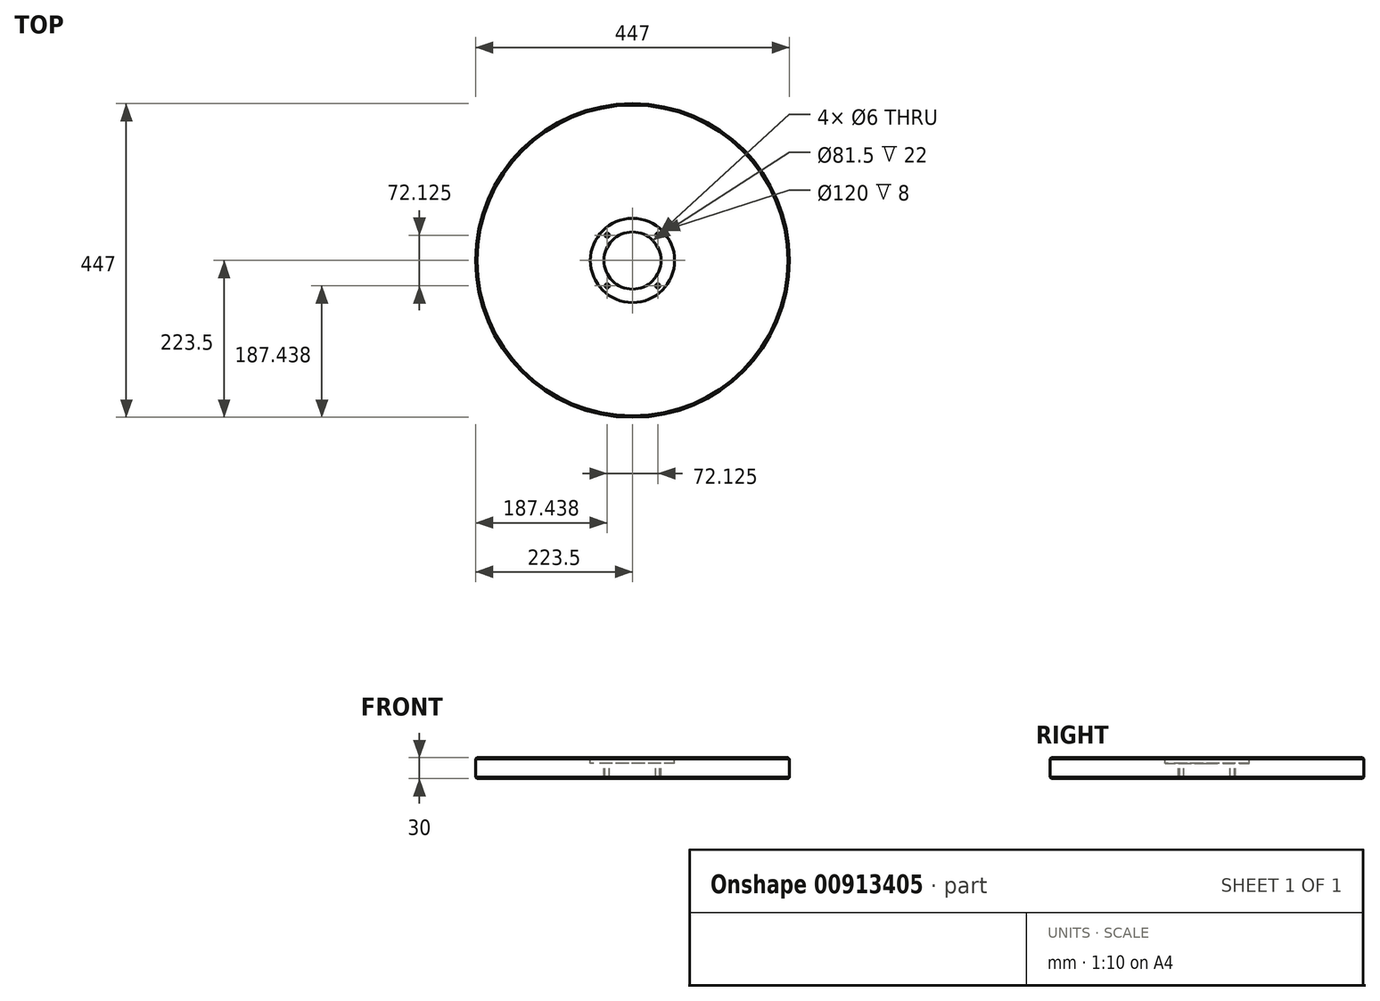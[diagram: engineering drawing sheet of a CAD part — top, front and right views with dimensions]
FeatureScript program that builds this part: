
annotation { "Feature Type Name" : "Feature", "Feature Type Description" : "" }
export const myFeature = defineFeature(function(context is Context, id is Id, definition is map)
    precondition{}
    {
        {
            var Q0;
            Q0=qCreatedBy(makeId("Top.planeOp"),FACE);
            var sketch = newSketch(context, id + "F0", { "sketchPlane" : qUnion([Q0])});
            skCircle(sketch, "E0", {"center": v(0, 0) * mm, "radius": 223.5 * mm});
            skSolve(sketch);
        }
        {
            var Q0;
            Q0=makeQuery(id+"F0.imprint","IMPRINT",FACE,{"disambiguationData":[TD([[makeQuery(id+"F0.imprint","IMPRINT",EDGE,{"derivedFrom":sQuery(id+"F0.wireOp",EDGE,"E0")}),1.0]])]});
            extrude(context, id + "F1", {"entities" : qUnion([Q0]), "depth" : 30 * mm, "offsetDistance" : 25 * mm});
        }
        {
            var Q0;
            Q0=makeQuery(id+"F1.opExtrude","CAP_EDGE",EDGE,{"disambiguationData":[OSD([sQuery(id+"F0.wireOp",EDGE,"E0")])],"isStart":false});
            var Q1;
            Q1=makeQuery(id+"F1.opExtrude","CAP_EDGE",EDGE,{"disambiguationData":[OSD([sQuery(id+"F0.wireOp",EDGE,"E0")])],"isStart":true});
            chamfer(context, id + "F2", {"entities" : qUnion([Q0, Q1]), "width" : 2 * mm, "tangentPropagation" : true});
        }
        {
            var Q0;
            Q0=makeQuery(id+"F1.opExtrude","CAP_FACE",FACE,{"disambiguationData":[OSD([sQuery(id+"F0.wireOp",EDGE,"E0")])],"isStart":false});
            var sketch = newSketch(context, id + "F3", { "sketchPlane" : qUnion([Q0])});
            skCircle(sketch, "E1", {"center": v(0, 0) * mm, "radius": 40.75 * mm});
            skCircle(sketch, "E2", {"center": v(0, 0) * mm, "radius": 51 * mm, "construction": true});
            skCircle(sketch, "E3", {"center": v(0, 0) * mm, "radius": 60 * mm});
            skLineSegment(sketch, "E4", {"start": v(63.69, 0) * mm, "end": v(0, 0) * mm, "construction": true});
            skLineSegment(sketch, "E5", {"start": v(0, 0) * mm, "end": v(21.66, 21.66) * mm, "construction": true});
            skCircle(sketch, "E6", {"center": v(36.06, 36.06) * mm, "radius": 3 * mm});
            skCircle(sketch, "E7.1.0", {"center": v(-36.06, 36.06) * mm, "radius": 3 * mm});
            skCircle(sketch, "E7.2.0", {"center": v(-36.06, -36.06) * mm, "radius": 3 * mm});
            skCircle(sketch, "E7.3.0", {"center": v(36.06, -36.06) * mm, "radius": 3 * mm});
            skSolve(sketch);
        }
        {
            var Q0;
            Q0=makeQuery(id+"F3.imprint","IMPRINT",FACE,{"disambiguationData":[TD([[makeQuery(id+"F3.imprint","IMPRINT",EDGE,{"derivedFrom":sQuery(id+"F3.wireOp",EDGE,"E1")}),1.0]])]});
            extrude(context, id + "F4", {"entities" : qUnion([Q0]), "operationType" : NewBodyOperationType.REMOVE, "oppositeDirection" : true, "depth" : 30 * mm, "offsetDistance" : 25 * mm});
        }
        {
            var Q0;
            Q0=makeQuery(id+"F3.imprint","IMPRINT",FACE,{"disambiguationData":[TD([[makeQuery(id+"F3.imprint","IMPRINT",EDGE,{"derivedFrom":sQuery(id+"F3.wireOp",EDGE,"E1")}),-1.0]])]});
            var Q1;
            Q1=makeQuery(id+"F3.imprint","IMPRINT",FACE,{"disambiguationData":[TD([[makeQuery(id+"F3.imprint","IMPRINT",EDGE,{"derivedFrom":sQuery(id+"F3.wireOp",EDGE,"E7.1.0")}),1.0]])]});
            var Q2;
            Q2=makeQuery(id+"F3.imprint","IMPRINT",FACE,{"disambiguationData":[TD([[makeQuery(id+"F3.imprint","IMPRINT",EDGE,{"derivedFrom":sQuery(id+"F3.wireOp",EDGE,"E6")}),1.0]])]});
            var Q3;
            Q3=makeQuery(id+"F3.imprint","IMPRINT",FACE,{"disambiguationData":[TD([[makeQuery(id+"F3.imprint","IMPRINT",EDGE,{"derivedFrom":sQuery(id+"F3.wireOp",EDGE,"E7.3.0")}),1.0]])]});
            var Q4;
            Q4=makeQuery(id+"F3.imprint","IMPRINT",FACE,{"disambiguationData":[TD([[makeQuery(id+"F3.imprint","IMPRINT",EDGE,{"derivedFrom":sQuery(id+"F3.wireOp",EDGE,"E7.2.0")}),1.0]])]});
            extrude(context, id + "F5", {"entities" : qUnion([Q0, Q1, Q2, Q3, Q4]), "operationType" : NewBodyOperationType.REMOVE, "oppositeDirection" : true, "depth" : 8 * mm, "offsetDistance" : 25 * mm});
        }
        {
            var Q0;
            Q0=makeQuery(id+"F3.imprint","IMPRINT",FACE,{"disambiguationData":[TD([[makeQuery(id+"F3.imprint","IMPRINT",EDGE,{"derivedFrom":sQuery(id+"F3.wireOp",EDGE,"E7.1.0")}),1.0]])]});
            var Q1;
            Q1=makeQuery(id+"F3.imprint","IMPRINT",FACE,{"disambiguationData":[TD([[makeQuery(id+"F3.imprint","IMPRINT",EDGE,{"derivedFrom":sQuery(id+"F3.wireOp",EDGE,"E6")}),1.0]])]});
            var Q2;
            Q2=makeQuery(id+"F3.imprint","IMPRINT",FACE,{"disambiguationData":[TD([[makeQuery(id+"F3.imprint","IMPRINT",EDGE,{"derivedFrom":sQuery(id+"F3.wireOp",EDGE,"E7.3.0")}),1.0]])]});
            var Q3;
            Q3=makeQuery(id+"F3.imprint","IMPRINT",FACE,{"disambiguationData":[TD([[makeQuery(id+"F3.imprint","IMPRINT",EDGE,{"derivedFrom":sQuery(id+"F3.wireOp",EDGE,"E7.2.0")}),1.0]])]});
            extrude(context, id + "F6", {"entities" : qUnion([Q0, Q1, Q2, Q3]), "operationType" : NewBodyOperationType.REMOVE, "endBound" : BoundingType.THROUGH_ALL, "oppositeDirection" : true, "depth" : 25 * mm, "offsetDistance" : 25 * mm});
        }
    });
